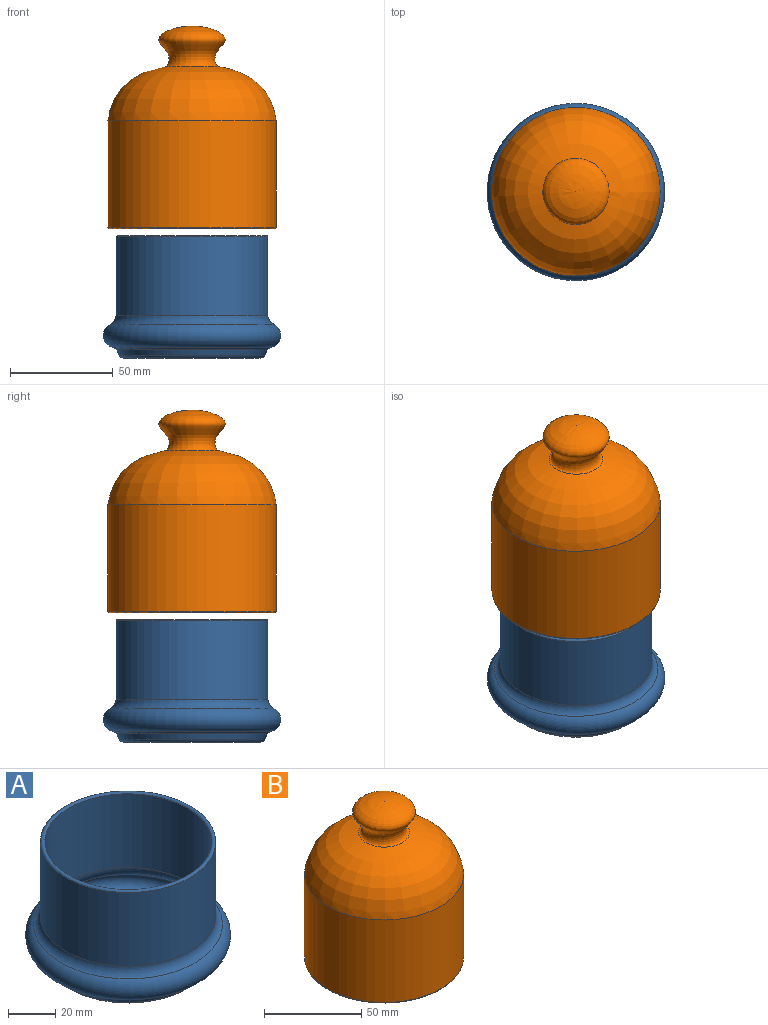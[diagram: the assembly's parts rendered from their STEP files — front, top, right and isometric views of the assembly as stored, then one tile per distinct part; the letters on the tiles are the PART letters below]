
ASSEMBLY  parts=2 mates=1
PART A: 15 faces, bbox 93.5x93.5x59.6 mm
  f0: plane 67.17x67.17mm, normal (0,0,1), area 3543.5mm2, adj f14
  f1: plane 67.17x67.17mm, normal (0,0,-1), area 3543.5mm2, adj f2
  f2: torus R=33.58mm, axis (0,0,1), area 491.9mm2, adj f1,f3
  f3: cone r=35.39mm half-angle=25.2deg, axis (0,0,1), area 704.8mm2, adj f2,f4
  f4: torus R=38.53mm, axis (0,0,1), area 453.3mm2, adj f3,f5
  f5: torus R=37.21mm, axis (0,0,1), area 3968.1mm2, adj f4,f6
  f6: torus R=42mm, axis (0,0,1), area 1336.3mm2, adj f5,f7
  f7: cylinder r=37mm len=74mm, axis (0,0,1), area 8856.4mm2, adj f6,f8
  f8: torus R=36.05mm, axis (0,0,1), area 537mm2, adj f7,f9
  f9: cylinder r=35.1mm len=70.2mm, axis (0,0,1), area 8401.6mm2, adj f8,f10
  f10: torus R=42mm, axis (0,0,1), area 1770mm2, adj f9,f11
  f11: torus R=37.21mm, axis (0,0,1), area 2619.2mm2, adj f10,f12
  f12: torus R=38.53mm, axis (0,0,1), area 857.8mm2, adj f11,f13
  f13: cone r=33.68mm half-angle=25.2deg, axis (0,0,1), area 671.2mm2, adj f12,f14
  f14: torus R=33.58mm, axis (0,0,1), area 23.9mm2, adj f0,f13
PART B: 7 faces, bbox 88.7x88.7x98.7 mm
  f0: revolved ~32.34x32.34mm, area 2296.2mm2, adj f6
  f1: revolved ~29.74x29.74mm, area 2077.3mm2, adj f2
  f2: revolved ~79.39x79.39mm, area 7102.1mm2, adj f1,f3
  f3: cylinder r=39.7mm len=79.39mm, axis (0,0,1), area 13215.9mm2, adj f2,f4
  f4: torus R=40.35mm, axis (0,0,1), area 517.7mm2, adj f3,f5
  f5: cylinder r=41mm len=81.99mm, axis (0,0,1), area 13394.4mm2, adj f4,f6
  f6: revolved ~81.99x81.99mm, area 7874.5mm2, adj f0,f5
PLACE A t=(3.71,-48.88,-4.6)mm
PLACE B t=(-68.63,-48.88,66.07)mm
MATE slider B.f3 <-> A.f2  axis (0,0,1) through (-51.23,-48.88,70.42)mm
